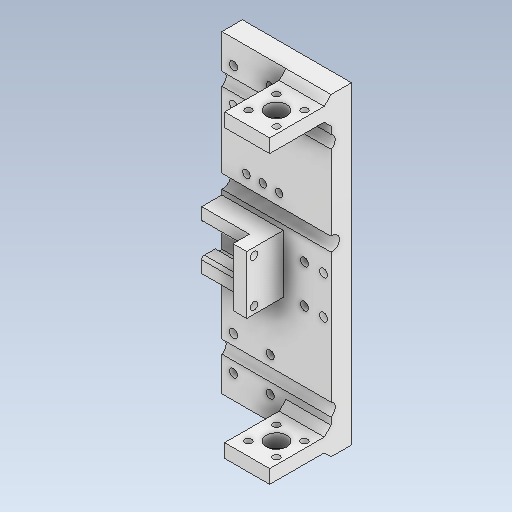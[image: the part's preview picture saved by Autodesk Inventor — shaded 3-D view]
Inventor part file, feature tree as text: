
AUTODESK INVENTOR PART (.ipt)
format: ipt  version: 2020 (Build 240168000, 168)  size: 338,432 bytes
history: native  units: mm
features: reference x13, sketch x10, other x10, extrude x9, hole x2, fillet x1, mirror x1, chamfer x1, projected_geometry x1
ambient origin geometry x8: Origin, YZ Plane, XZ Plane, XY Plane, X Axis, Y Axis, Z Axis, Center Point
bodies: Solid1 (feature_tree)
feature tree (48):
  extrude  "Extrusion1"  Depth=80.0mm
  extrude  "Extrusion2"  Depth=15.0mm
  extrude  "Extrusion3"  Depth=2.0mm
  extrude  "Extrusion4"  Depth=2.0mm
  fillet  "Fillet1"  [1 undecoded]
  extrude  "Extrusion5"  Depth=10.3mm
  hole  "Hole1"  [1 undecoded]
  extrude  "Extrusion6"  Depth=4.8mm
  extrude  "Extrusion7"  Depth=105.0mm
  extrude  "Extrusion8"  Depth=10.0mm
  mirror  "Mirror2"
  hole  "Hole2"  [1 undecoded]
  chamfer  "Chamfer4"  Distance=2.0mm
  extrude  "Extrusion10"  Depth=12.0mm
  sketch  "Sketch1"  dims[d0=230.0mm d1=80.0mm]
  sketch  "Sketch2"  dims[d2=15.0mm d3=0.0mm d4=10.3mm]
  sketch  "Sketch3"  dims[d5=2.0mm d6=30.0mm]
  sketch  "Sketch5"  dims[d7=2.0mm d8=30.0mm d9=0.0mm d10=0.0mm]
  sketch  "Sketch6"  dims[d11=1.0mm d12=10.3mm]
  sketch  "Sketch7"  dims[d13=135.0mm d14=25.0mm d15=0.0mm]
  reference  "Reference11"
  reference  "Reference12"
  sketch  "Sketch8"  dims[d20=26.5mm d21=4.8mm]
  sketch  "Sketch10"  dims[d29=2.7mm d30=10.0mm]
  projected_geometry  "Projected Loop1"
  reference  "Reference18"
  reference  "Reference19"
  reference  "Reference20"
  reference  "Reference21"
  reference  "Reference22"
  reference  "Reference23"
  reference  "Reference24"
  reference  "Reference25"
  sketch  "Sketch13"  dims[d31=8.0mm d32=35.0mm d33=0.0mm d34=2.0mm d35=12.0mm d36=10.0mm d37=0.0mm d38=5.5mm d39=6.0mm d40=4.0mm d41=2.0mm d42=90.0deg d43=8.0mm d44=20.594885mm d47=33.0mm d48=5.0mm d49=10.0mm d50=45.0mm d51=0.0mm d55=20.506097mm d59=15.0mm d61=20.506097mm d62=5.0mm d63=4.746952mm d65=20.0mm d66=18.0mm d67=113.25mm d68=0.0mm d78=9.0mm d79=35.0mm d80=0.0mm d82=5.5mm d84=86.0mm d85=14.0mm d86=28.0mm d87=5.0mm d88=6.0mm d89=6.0mm d90=11.0mm d91=2.0mm d92=90.0deg d93=8.0mm d94=20.594885mm d95=10.253048mm d96=5.0mm d97=2.0mm d98=45.0deg d103=0.0mm d104=0.0mm]
  reference  "Reference26"
  reference  "Reference27"
  reference  "Reference28"
  other  "<path> 2.1 Aracet.iam"
  other  "I.A.B 2.1 Aracet.iam"
  other  "0008-10-012 Intinzator X.ipt:17"
  sketch  "Sketch9"  dims[d26=13.25mm d28=105.0mm]
  other  "0008-10-010 Fixare AxaX:6"
  other  "0008-10-010 Fixare AxaX:7"
  other  "0008-10-010 Fixare AxaX:3"
  other  "0008-10-010 Fixare AxaX:5"
  parser-record x1  (decoder bookkeeping rows leaked as tree rows — omitted from the tree; the rows remain in map.json)
  other  "0008-10-02 X Axis.iam"
  other  "0008-10-011 Fixare AxaX Mijloc.ipt:54"
note: 3 required parameter values undecoded (feature->parameter linkage not recoverable at this tier; creation-order binding heuristic only, values carry confidence <= 0.55)
note: 2 file-system paths scrubbed to <path> (originals preserved in map.json)
